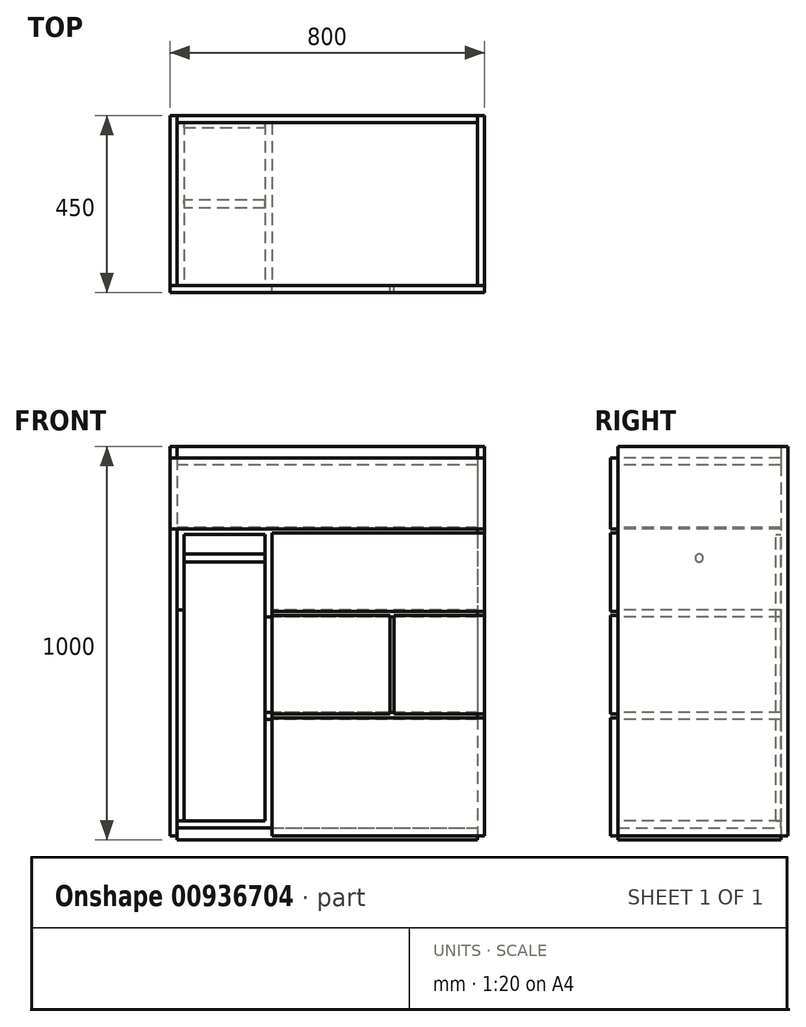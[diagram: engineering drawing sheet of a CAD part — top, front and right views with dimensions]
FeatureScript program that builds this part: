
annotation { "Feature Type Name" : "Feature", "Feature Type Description" : "" }
export const myFeature = defineFeature(function(context is Context, id is Id, definition is map)
    precondition{}
    {
        {
            var Q0;
            Q0=qCreatedBy(makeId("Top.planeOp"),FACE);
            var sketch = newSketch(context, id + "F0", { "sketchPlane" : qUnion([Q0])});
            skLineSegment(sketch, "E0.bottom", {"start": v(0, 0) * mm, "end": v(800, 0) * mm});
            skLineSegment(sketch, "E0.top", {"start": v(0, 432) * mm, "end": v(800, 432) * mm});
            skLineSegment(sketch, "E0.left", {"start": v(0, 0) * mm, "end": v(0, 432) * mm});
            skLineSegment(sketch, "E0.right", {"start": v(800, 0) * mm, "end": v(800, 432) * mm});
            skLineSegment(sketch, "E1.0", {"start": v(18, 0) * mm, "end": v(18, 432) * mm});
            skLineSegment(sketch, "E2", {"start": v(400, 467.89) * mm, "end": v(400, 549.02) * mm, "construction": true});
            skPoint(sketch, "E2.startSnap0", {"position": v(400, 432) * mm});
            skLineSegment(sketch, "E3.MirrorCS", {"start": v(782, 0) * mm, "end": v(782, 432) * mm});
            skLineSegment(sketch, "E4", {"start": v(828.28, 216) * mm, "end": v(900.38, 216) * mm, "construction": true});
            skPoint(sketch, "E4.startSnap0", {"position": v(800, 216) * mm});
            skLineSegment(sketch, "E5.0", {"start": v(0, 414) * mm, "end": v(800, 414) * mm});
            skSolve(sketch);
        }
        {
            var Q0;
            {var subQ0=sQuery(id+"F0.wireOp",EDGE,"E0.left");var subQ1=sQuery(id+"F0.wireOp",EDGE,"E0.bottom");var subQ2=makeQuery(id+"F0.imprint","INTERSECT",VERTEX,{"derivedFrom":[subQ1,subQ0]});Q0=makeQuery(id+"F0.imprint","IMPRINT",FACE,{"disambiguationData":[TD([[makeQuery(id+"F0.imprint","IMPRINT",EDGE,{"disambiguationData":[TD([[subQ2,-1.0]])],"derivedFrom":subQ1}),1.0]])]});}
            var Q1;
            {var subQ0=sQuery(id+"F0.wireOp",EDGE,"E0.left");var subQ1=sQuery(id+"F0.wireOp",EDGE,"E0.top");var subQ2=makeQuery(id+"F0.imprint","INTERSECT",VERTEX,{"derivedFrom":[subQ1,subQ0]});Q1=makeQuery(id+"F0.imprint","IMPRINT",FACE,{"disambiguationData":[TD([[makeQuery(id+"F0.imprint","IMPRINT",EDGE,{"disambiguationData":[TD([[subQ2,-1.0]])],"derivedFrom":subQ1}),-1.0]])]});}
            var Q2;
            {var subQ0=sQuery(id+"F0.wireOp",EDGE,"E0.right");var subQ1=sQuery(id+"F0.wireOp",EDGE,"E0.top");var subQ2=makeQuery(id+"F0.imprint","INTERSECT",VERTEX,{"derivedFrom":[subQ1,subQ0]});Q2=makeQuery(id+"F0.imprint","IMPRINT",FACE,{"disambiguationData":[TD([[makeQuery(id+"F0.imprint","IMPRINT",EDGE,{"disambiguationData":[TD([[subQ2,1.0]])],"derivedFrom":subQ1}),-1.0]])]});}
            var Q3;
            {var subQ0=sQuery(id+"F0.wireOp",EDGE,"E0.right");var subQ1=sQuery(id+"F0.wireOp",EDGE,"E0.bottom");var subQ2=makeQuery(id+"F0.imprint","INTERSECT",VERTEX,{"derivedFrom":[subQ1,subQ0]});Q3=makeQuery(id+"F0.imprint","IMPRINT",FACE,{"disambiguationData":[TD([[makeQuery(id+"F0.imprint","IMPRINT",EDGE,{"disambiguationData":[TD([[subQ2,1.0]])],"derivedFrom":subQ1}),1.0]])]});}
            extrude(context, id + "F1", {"entities" : qUnion([Q0, Q1, Q2, Q3]), "depth" : 990 * mm, "offsetDistance" : 25 * mm});
        }
        {
            var Q0;
            {var subQ0=sQuery(id+"F0.wireOp",EDGE,"E1.0");var subQ1=sQuery(id+"F0.wireOp",EDGE,"E0.top");var subQ2=makeQuery(id+"F0.imprint","INTERSECT",VERTEX,{"derivedFrom":[subQ1,subQ0]});Q0=makeQuery(id+"F0.imprint","IMPRINT",FACE,{"disambiguationData":[TD([[makeQuery(id+"F0.imprint","IMPRINT",EDGE,{"disambiguationData":[TD([[subQ2,-1.0]])],"derivedFrom":subQ1}),-1.0]])]});}
            var Q1;
            Q1=makeQuery(id+"F1.opExtrude","CAP_FACE",FACE,{"disambiguationData":[OSD([sQuery(id+"F0.wireOp",EDGE,"E0.bottom"),sQuery(id+"F0.wireOp",EDGE,"E0.top"),sQuery(id+"F0.wireOp",EDGE,"E0.left"),sQuery(id+"F0.wireOp",EDGE,"E1.0")])],"isStart":false});
            extrude(context, id + "F2", {"entities" : qUnion([Q0]), "endBound" : BoundingType.UP_TO_SURFACE, "depth" : 25 * mm, "endBoundEntityFace" : qUnion([Q1]), "offsetDistance" : 25 * mm});
        }
        {
            var Q0;
            {var subQ0=sQuery(id+"F0.wireOp",EDGE,"E1.0");var subQ1=sQuery(id+"F0.wireOp",EDGE,"E0.bottom");var subQ2=makeQuery(id+"F0.imprint","INTERSECT",VERTEX,{"derivedFrom":[subQ1,subQ0]});Q0=makeQuery(id+"F0.imprint","IMPRINT",FACE,{"disambiguationData":[TD([[makeQuery(id+"F0.imprint","IMPRINT",EDGE,{"disambiguationData":[TD([[subQ2,-1.0]])],"derivedFrom":subQ1}),1.0]])]});}
            extrude(context, id + "F3", {"entities" : qUnion([Q0]), "depth" : 20 * mm, "offsetDistance" : 25 * mm, "hasSecondDirection" : true, "secondDirectionOppositeDirection" : true, "secondDirectionDepth" : 10 * mm});
        }
        {
            var Q0;
            {var subQ0=sQuery(id+"F0.wireOp",EDGE,"E0.bottom");Q0=makeQuery(id+"F1.opExtrude","SWEPT_FACE",FACE,{"disambiguationData":[OSD([subQ0]),TDD([makeQuery(id+"F0.imprint","IMPRINT",EDGE,{"disambiguationData":[TD([[makeQuery(id+"F0.imprint","INTERSECT",VERTEX,{"derivedFrom":[subQ0,sQuery(id+"F0.wireOp",EDGE,"E0.left")]}),-1.0]])],"derivedFrom":subQ0})])]});}
            var sketch = newSketch(context, id + "F4", { "sketchPlane" : qUnion([Q0])});
            skLineSegment(sketch, "E6.bottom", {"start": v(800, 560) * mm, "end": v(570, 560) * mm});
            skLineSegment(sketch, "E6.top", {"start": v(800, 310) * mm, "end": v(570, 310) * mm});
            skLineSegment(sketch, "E6.left", {"start": v(800, 560) * mm, "end": v(800, 310) * mm});
            skLineSegment(sketch, "E6.right", {"start": v(570, 560) * mm, "end": v(570, 310) * mm});
            skLineSegment(sketch, "E7.bottom", {"start": v(560, 560) * mm, "end": v(0, 560) * mm});
            skLineSegment(sketch, "E7.top", {"start": v(560, 310) * mm, "end": v(0, 310) * mm});
            skLineSegment(sketch, "E7.left", {"start": v(560, 560) * mm, "end": v(560, 310) * mm});
            skLineSegment(sketch, "E7.right", {"start": v(0, 560) * mm, "end": v(0, 310) * mm});
            skLineSegment(sketch, "E8", {"start": v(570, 435) * mm, "end": v(560, 435) * mm, "construction": true});
            skLineSegment(sketch, "E9.bottom", {"start": v(0, 300) * mm, "end": v(250, 300) * mm});
            skLineSegment(sketch, "E9.top", {"start": v(0, 0) * mm, "end": v(250, 0) * mm});
            skLineSegment(sketch, "E9.right", {"start": v(250, 300) * mm, "end": v(250, 0) * mm});
            skLineSegment(sketch, "E10.bottom", {"start": v(260, 300) * mm, "end": v(800, 300) * mm});
            skLineSegment(sketch, "E10.top", {"start": v(260, 0) * mm, "end": v(800, 0) * mm});
            skLineSegment(sketch, "E10.left", {"start": v(260, 300) * mm, "end": v(260, 0) * mm});
            skLineSegment(sketch, "E10.right", {"start": v(800, 300) * mm, "end": v(800, 0) * mm});
            skLineSegment(sketch, "E11", {"start": v(10.26, 310) * mm, "end": v(10.26, 300) * mm, "construction": true});
            skLineSegment(sketch, "E12", {"start": v(260, 150) * mm, "end": v(250, 150) * mm, "construction": true});
            skLineSegment(sketch, "E13.bottom", {"start": v(800, 770) * mm, "end": v(260, 770) * mm});
            skLineSegment(sketch, "E13.top", {"start": v(800, 570) * mm, "end": v(260, 570) * mm});
            skLineSegment(sketch, "E13.left", {"start": v(800, 770) * mm, "end": v(800, 570) * mm});
            skLineSegment(sketch, "E13.right", {"start": v(260, 770) * mm, "end": v(260, 570) * mm});
            skLineSegment(sketch, "E14.bottom", {"start": v(250, 770) * mm, "end": v(0, 770) * mm});
            skLineSegment(sketch, "E14.top", {"start": v(250, 570) * mm, "end": v(0, 570) * mm});
            skLineSegment(sketch, "E14.left", {"start": v(250, 770) * mm, "end": v(250, 570) * mm});
            skLineSegment(sketch, "E14.right", {"start": v(0, 770) * mm, "end": v(0, 570) * mm});
            skLineSegment(sketch, "E15", {"start": v(277.64, 570) * mm, "end": v(277.64, 560) * mm, "construction": true});
            skLineSegment(sketch, "E16", {"start": v(260, 629.54) * mm, "end": v(250, 629.54) * mm, "construction": true});
            skLineSegment(sketch, "E17.bottom", {"start": v(0, 990) * mm, "end": v(800, 990) * mm});
            skLineSegment(sketch, "E17.top", {"start": v(0, 780) * mm, "end": v(800, 780) * mm});
            skLineSegment(sketch, "E17.left", {"start": v(0, 990) * mm, "end": v(0, 780) * mm});
            skLineSegment(sketch, "E17.right", {"start": v(800, 990) * mm, "end": v(800, 780) * mm});
            skLineSegment(sketch, "E18", {"start": v(-67.03, 780) * mm, "end": v(-67.03, 770) * mm, "construction": true});
            skLineSegment(sketch, "E19", {"start": v(0, 300) * mm, "end": v(0, 0) * mm});
            skLineSegment(sketch, "E20", {"start": v(0, 960) * mm, "end": v(800, 960) * mm});
            skLineSegment(sketch, "E21", {"start": v(260, 560) * mm, "end": v(260, 310) * mm});
            skSolve(sketch);
        }
        {
            var Q0;
            {var subQ0=sQuery(id+"F4.wireOp",EDGE,"E17.right");var subQ1=sQuery(id+"F4.wireOp",EDGE,"E17.top");var subQ2=makeQuery(id+"F4.imprint","INTERSECT",VERTEX,{"derivedFrom":[subQ1,subQ0]});Q0=makeQuery(id+"F4.imprint","IMPRINT",FACE,{"disambiguationData":[TD([[makeQuery(id+"F4.imprint","IMPRINT",EDGE,{"disambiguationData":[TD([[subQ2,1.0]])],"derivedFrom":subQ0}),-1.0]])]});}
            var Q1;
            {var subQ0=sQuery(id+"F4.wireOp",EDGE,"E17.left");var subQ6=sQuery(id+"F4.wireOp",EDGE,"E20");var subQ7=makeQuery(id+"F4.imprint","INTERSECT",VERTEX,{"derivedFrom":[subQ0,subQ6]});Q1=makeQuery(id+"F4.imprint","IMPRINT",FACE,{"disambiguationData":[TD([[makeQuery(id+"F4.imprint","IMPRINT",EDGE,{"disambiguationData":[TD([[subQ7,-1.0]])],"derivedFrom":subQ6}),-1.0]])]});}
            var Q2;
            Q2=makeQuery(id+"F4.imprint","IMPRINT",FACE,{"disambiguationData":[TD([[makeQuery(id+"F4.imprint","IMPRINT",EDGE,{"derivedFrom":sQuery(id+"F4.wireOp",EDGE,"E13.bottom")}),1.0]])]});
            var Q3;
            Q3=makeQuery(id+"F4.imprint","IMPRINT",FACE,{"disambiguationData":[TD([[makeQuery(id+"F4.imprint","IMPRINT",EDGE,{"derivedFrom":sQuery(id+"F4.wireOp",EDGE,"E6.bottom")}),1.0]])]});
            var Q4;
            Q4=makeQuery(id+"F4.imprint","IMPRINT",FACE,{"disambiguationData":[TD([[makeQuery(id+"F4.imprint","IMPRINT",EDGE,{"derivedFrom":sQuery(id+"F4.wireOp",EDGE,"E10.bottom")}),-1.0]])]});
            var Q5;
            {var subQ0=sQuery(id+"F4.wireOp",EDGE,"E7.left");Q5=makeQuery(id+"F4.imprint","IMPRINT",FACE,{"disambiguationData":[TD([[makeQuery(id+"F4.imprint","IMPRINT",EDGE,{"derivedFrom":subQ0}),-1.0]])]});}
            extrude(context, id + "F5", {"entities" : qUnion([Q0, Q1, Q2, Q3, Q4, Q5]), "depth" : 18 * mm, "offsetDistance" : 25 * mm});
        }
        {
            var Q0;
            Q0=makeQuery(id+"F5.opExtrude","CAP_FACE",FACE,{"disambiguationData":[OSD([sQuery(id+"F4.wireOp",EDGE,"E17.top"),sQuery(id+"F4.wireOp",EDGE,"E17.left"),sQuery(id+"F4.wireOp",EDGE,"E17.right"),sQuery(id+"F4.wireOp",EDGE,"E20")])],"isStart":true});
            var sketch = newSketch(context, id + "F6", { "sketchPlane" : qUnion([Q0])});
            skLineSegment(sketch, "E22.bottom", {"start": v(-782, 784) * mm, "end": v(-18, 784) * mm});
            skLineSegment(sketch, "E22.top", {"start": v(-782, 766) * mm, "end": v(-18, 766) * mm});
            skLineSegment(sketch, "E22.left", {"start": v(-782, 784) * mm, "end": v(-782, 766) * mm});
            skLineSegment(sketch, "E22.right", {"start": v(-18, 784) * mm, "end": v(-18, 766) * mm});
            skLineSegment(sketch, "E23", {"start": v(-903.66, 780) * mm, "end": v(-903.66, 770) * mm, "construction": true});
            skLineSegment(sketch, "E24", {"start": v(-878.2, 570) * mm, "end": v(-878.2, 560) * mm, "construction": true});
            skLineSegment(sketch, "E25", {"start": v(-871.46, 310) * mm, "end": v(-871.46, 300) * mm, "construction": true});
            skLineSegment(sketch, "E26", {"start": v(-570, 442.76) * mm, "end": v(-560, 442.76) * mm, "construction": true});
            skLineSegment(sketch, "E27", {"start": v(-260, 157.99) * mm, "end": v(-242, 157.99) * mm, "construction": true});
            skPoint(sketch, "E28", {"position": v(-903.66, 775) * mm});
            skPoint(sketch, "E29", {"position": v(-878.2, 565) * mm});
            skPoint(sketch, "E30", {"position": v(-565, 442.76) * mm});
            skPoint(sketch, "E31", {"position": v(-871.46, 305) * mm});
            skPoint(sketch, "E32", {"position": v(-251, 157.99) * mm});
            skPoint(sketch, "E33", {"position": v(-782, 775) * mm});
            skLineSegment(sketch, "E34.bottom", {"start": v(-782, 574) * mm, "end": v(-18, 574) * mm});
            skLineSegment(sketch, "E34.top", {"start": v(-782, 556) * mm, "end": v(-18, 556) * mm});
            skLineSegment(sketch, "E34.left", {"start": v(-782, 574) * mm, "end": v(-782, 556) * mm});
            skLineSegment(sketch, "E34.right", {"start": v(-18, 574) * mm, "end": v(-18, 556) * mm});
            skLineSegment(sketch, "E35.bottom", {"start": v(-782, 314) * mm, "end": v(-18, 314) * mm});
            skLineSegment(sketch, "E35.top", {"start": v(-782, 296) * mm, "end": v(-18, 296) * mm});
            skLineSegment(sketch, "E35.left", {"start": v(-782, 314) * mm, "end": v(-782, 296) * mm});
            skLineSegment(sketch, "E35.right", {"start": v(-18, 314) * mm, "end": v(-18, 296) * mm});
            skLineSegment(sketch, "E36.bottom", {"start": v(-260, 296) * mm, "end": v(-242, 296) * mm});
            skLineSegment(sketch, "E36.top", {"start": v(-260, 20) * mm, "end": v(-242, 20) * mm});
            skLineSegment(sketch, "E36.left", {"start": v(-260, 296) * mm, "end": v(-260, 20) * mm});
            skLineSegment(sketch, "E36.right", {"start": v(-242, 296) * mm, "end": v(-242, 20) * mm});
            skLineSegment(sketch, "E37.bottom", {"start": v(-574, 556) * mm, "end": v(-556, 556) * mm});
            skLineSegment(sketch, "E37.top", {"start": v(-574, 314) * mm, "end": v(-556, 314) * mm});
            skLineSegment(sketch, "E37.left", {"start": v(-574, 556) * mm, "end": v(-574, 314) * mm});
            skLineSegment(sketch, "E37.right", {"start": v(-556, 556) * mm, "end": v(-556, 314) * mm});
            skLineSegment(sketch, "E38.bottom", {"start": v(-260, 766) * mm, "end": v(-242, 766) * mm});
            skLineSegment(sketch, "E38.top", {"start": v(-260, 574) * mm, "end": v(-242, 574) * mm});
            skLineSegment(sketch, "E38.left", {"start": v(-260, 766) * mm, "end": v(-260, 574) * mm});
            skLineSegment(sketch, "E38.right", {"start": v(-242, 766) * mm, "end": v(-242, 574) * mm});
            skLineSegment(sketch, "E39.bottom", {"start": v(-36, 766) * mm, "end": v(-18, 766) * mm});
            skLineSegment(sketch, "E39.top", {"start": v(-36, 574) * mm, "end": v(-18, 574) * mm});
            skLineSegment(sketch, "E39.left", {"start": v(-36, 766) * mm, "end": v(-36, 574) * mm});
            skLineSegment(sketch, "E39.right", {"start": v(-18, 766) * mm, "end": v(-18, 574) * mm});
            skPoint(sketch, "E40", {"position": v(-782, 565) * mm});
            skPoint(sketch, "E41", {"position": v(-565, 556) * mm});
            skPoint(sketch, "E42", {"position": v(-782, 305) * mm});
            skPoint(sketch, "E43", {"position": v(-251, 296) * mm});
            skLineSegment(sketch, "E44.bottom", {"start": v(-782, 960) * mm, "end": v(-18, 960) * mm});
            skLineSegment(sketch, "E44.top", {"start": v(-782, 942) * mm, "end": v(-18, 942) * mm});
            skLineSegment(sketch, "E44.left", {"start": v(-782, 960) * mm, "end": v(-782, 942) * mm});
            skLineSegment(sketch, "E44.right", {"start": v(-18, 960) * mm, "end": v(-18, 942) * mm});
            skLineSegment(sketch, "E45", {"start": v(-260, 574) * mm, "end": v(-260, 296) * mm});
            skLineSegment(sketch, "E46", {"start": v(-242, 574) * mm, "end": v(-242, 296) * mm});
            skLineSegment(sketch, "E47", {"start": v(-36, 574) * mm, "end": v(-36, 20) * mm});
            skLineSegment(sketch, "E48", {"start": v(-36, 20) * mm, "end": v(-18, 20) * mm});
            skLineSegment(sketch, "E49", {"start": v(-18, 20) * mm, "end": v(-18, 556) * mm});
            skLineSegment(sketch, "E50", {"start": v(-260, 38) * mm, "end": v(-18, 38) * mm});
            skLineSegment(sketch, "E51", {"start": v(-260, 20) * mm, "end": v(-18, 20) * mm});
            skSolve(sketch);
        }
        {
            var Q0;
            Q0=makeQuery(id+"F6.imprint","IMPRINT",FACE,{"disambiguationData":[TD([[makeQuery(id+"F6.imprint","IMPRINT",EDGE,{"derivedFrom":sQuery(id+"F6.wireOp",EDGE,"E44.bottom")}),1.0]])]});
            var Q1;
            {var subQ6=sQuery(id+"F6.wireOp",EDGE,"E38.bottom");Q1=makeQuery(id+"F6.imprint","IMPRINT",FACE,{"disambiguationData":[TD([[makeQuery(id+"F6.imprint","IMPRINT",EDGE,{"derivedFrom":subQ6}),1.0]])]});}
            var Q2;
            {var subQ0=sQuery(id+"F6.wireOp",EDGE,"E22.bottom");Q2=makeQuery(id+"F6.imprint","IMPRINT",FACE,{"disambiguationData":[TD([[makeQuery(id+"F6.imprint","IMPRINT",EDGE,{"derivedFrom":subQ0}),-1.0]])]});}
            var Q3;
            {var subQ4=sQuery(id+"F6.wireOp",EDGE,"E34.left");Q3=makeQuery(id+"F6.imprint","IMPRINT",FACE,{"disambiguationData":[TD([[makeQuery(id+"F6.imprint","IMPRINT",EDGE,{"derivedFrom":subQ4}),1.0]])]});}
            var Q4;
            {var subQ3=sQuery(id+"F6.wireOp",EDGE,"E35.left");Q4=makeQuery(id+"F6.imprint","IMPRINT",FACE,{"disambiguationData":[TD([[makeQuery(id+"F6.imprint","IMPRINT",EDGE,{"derivedFrom":subQ3}),1.0]])]});}
            var Q5;
            Q5=makeQuery(id+"F6.imprint","IMPRINT",FACE,{"disambiguationData":[TD([[makeQuery(id+"F6.imprint","IMPRINT",EDGE,{"derivedFrom":sQuery(id+"F6.wireOp",EDGE,"QM6Bufxx-I5ZU-JCkN-k9jX-k9IJHGgFzfra.bottom")}),1.0]])]});
            var Q6;
            {var subQ0=sQuery(id+"F6.wireOp",EDGE,"E51");var subQ1=sQuery(id+"F6.wireOp",EDGE,"E36.left");var subQ2=makeQuery(id+"F6.imprint","INTERSECT",VERTEX,{"derivedFrom":[subQ1,subQ0]});Q6=makeQuery(id+"F6.imprint","IMPRINT",FACE,{"disambiguationData":[TD([[makeQuery(id+"F6.imprint","IMPRINT",EDGE,{"disambiguationData":[TD([[subQ2,1.0]])],"derivedFrom":subQ1}),1.0]])]});}
            var Q7;
            {var subQ0=sQuery(id+"F6.wireOp",EDGE,"E51");var subQ1=sQuery(id+"F6.wireOp",EDGE,"E36.right");var subQ2=makeQuery(id+"F6.imprint","INTERSECT",VERTEX,{"derivedFrom":[subQ1,subQ0]});Q7=makeQuery(id+"F6.imprint","IMPRINT",FACE,{"disambiguationData":[TD([[makeQuery(id+"F6.imprint","IMPRINT",EDGE,{"disambiguationData":[TD([[subQ2,1.0]])],"derivedFrom":subQ1}),1.0]])]});}
            var Q8;
            {var subQ0=sQuery(id+"F6.wireOp",EDGE,"E51");var subQ1=sQuery(id+"F6.wireOp",EDGE,"E47");var subQ2=makeQuery(id+"F6.imprint","INTERSECT",VERTEX,{"derivedFrom":[subQ1,subQ0]});Q8=makeQuery(id+"F6.imprint","IMPRINT",FACE,{"disambiguationData":[TD([[makeQuery(id+"F6.imprint","IMPRINT",EDGE,{"disambiguationData":[TD([[subQ2,1.0]])],"derivedFrom":subQ1}),1.0]])]});}
            var Q9;
            Q9=makeQuery(id+"F2.opExtrude","SWEPT_FACE",FACE,{"disambiguationData":[OSD([sQuery(id+"F0.wireOp",EDGE,"E5.0")])]});
            extrude(context, id + "F7", {"entities" : qUnion([Q0, Q1, Q2, Q3, Q4, Q5, Q6, Q7, Q8]), "endBound" : BoundingType.UP_TO_SURFACE, "depth" : 25 * mm, "endBoundEntityFace" : qUnion([Q9]), "offsetDistance" : 25 * mm});
        }
        {
            var Q0;
            Q0=makeQuery(id+"F6.imprint","IMPRINT",FACE,{"disambiguationData":[TD([[makeQuery(id+"F6.imprint","IMPRINT",EDGE,{"derivedFrom":sQuery(id+"F6.wireOp",EDGE,"E38.bottom")}),-1.0]])]});
            var Q1;
            Q1=makeQuery(id+"F6.imprint","IMPRINT",FACE,{"disambiguationData":[TD([[makeQuery(id+"F6.imprint","IMPRINT",EDGE,{"derivedFrom":sQuery(id+"F6.wireOp",EDGE,"E37.bottom")}),-1.0]])]});
            var Q2;
            Q2=makeQuery(id+"F6.imprint","IMPRINT",FACE,{"disambiguationData":[TD([[makeQuery(id+"F6.imprint","IMPRINT",EDGE,{"derivedFrom":sQuery(id+"F6.wireOp",EDGE,"E36.bottom")}),-1.0]])]});
            var Q3;
            Q3=makeQuery(id+"F6.imprint","IMPRINT",FACE,{"disambiguationData":[TD([[makeQuery(id+"F6.imprint","IMPRINT",EDGE,{"derivedFrom":sQuery(id+"F6.wireOp",EDGE,"E39.bottom")}),-1.0]])]});
            var Q4;
            {var subQ5=sQuery(id+"F6.wireOp",EDGE,"E36.bottom");Q4=makeQuery(id+"F6.imprint","IMPRINT",FACE,{"disambiguationData":[TD([[makeQuery(id+"F6.imprint","IMPRINT",EDGE,{"derivedFrom":subQ5}),1.0]])]});}
            var Q5;
            {var subQ0=sQuery(id+"F6.wireOp",EDGE,"E45");var subQ1=sQuery(id+"F6.wireOp",EDGE,"E34.top");var subQ2=makeQuery(id+"F6.imprint","INTERSECT",VERTEX,{"derivedFrom":[subQ1,subQ0]});Q5=makeQuery(id+"F6.imprint","IMPRINT",FACE,{"disambiguationData":[TD([[makeQuery(id+"F6.imprint","IMPRINT",EDGE,{"disambiguationData":[TD([[subQ2,-1.0]])],"derivedFrom":subQ1}),-1.0]])]});}
            var Q6;
            {var subQ5=sQuery(id+"F6.wireOp",EDGE,"E38.top");Q6=makeQuery(id+"F6.imprint","IMPRINT",FACE,{"disambiguationData":[TD([[makeQuery(id+"F6.imprint","IMPRINT",EDGE,{"derivedFrom":subQ5}),-1.0]])]});}
            var Q7;
            {var subQ0=sQuery(id+"F6.wireOp",EDGE,"E34.right");Q7=makeQuery(id+"F6.imprint","IMPRINT",FACE,{"disambiguationData":[TD([[makeQuery(id+"F6.imprint","IMPRINT",EDGE,{"derivedFrom":subQ0}),-1.0]])]});}
            var Q8;
            {var subQ0=sQuery(id+"F6.wireOp",EDGE,"E49");var subQ5=sQuery(id+"F6.wireOp",EDGE,"E35.bottom");var subQ7=makeQuery(id+"F6.imprint","INTERSECT",VERTEX,{"derivedFrom":[subQ5,subQ0]});Q8=makeQuery(id+"F6.imprint","IMPRINT",FACE,{"disambiguationData":[TD([[makeQuery(id+"F6.imprint","IMPRINT",EDGE,{"disambiguationData":[TD([[subQ7,1.0]])],"derivedFrom":subQ5}),1.0]])]});}
            var Q9;
            {var subQ0=sQuery(id+"F6.wireOp",EDGE,"E49");var subQ1=sQuery(id+"F6.wireOp",EDGE,"E35.bottom");var subQ2=makeQuery(id+"F6.imprint","INTERSECT",VERTEX,{"derivedFrom":[subQ1,subQ0]});Q9=makeQuery(id+"F6.imprint","IMPRINT",FACE,{"disambiguationData":[TD([[makeQuery(id+"F6.imprint","IMPRINT",EDGE,{"disambiguationData":[TD([[subQ2,1.0]])],"derivedFrom":subQ1}),-1.0]])]});}
            var Q10;
            {var subQ0=sQuery(id+"F6.wireOp",EDGE,"E49");var subQ1=sQuery(id+"F6.wireOp",EDGE,"E35.top");var subQ2=makeQuery(id+"F6.imprint","INTERSECT",VERTEX,{"derivedFrom":[subQ1,subQ0]});Q10=makeQuery(id+"F6.imprint","IMPRINT",FACE,{"disambiguationData":[TD([[makeQuery(id+"F6.imprint","IMPRINT",EDGE,{"disambiguationData":[TD([[subQ2,1.0]])],"derivedFrom":subQ1}),-1.0]])]});}
            var Q11;
            Q11=makeQuery(id+"F7.opExtrude","CAP_FACE",FACE,{"disambiguationData":[OSD([sQuery(id+"F6.wireOp",EDGE,"E34.bottom"),sQuery(id+"F6.wireOp",EDGE,"E34.top"),sQuery(id+"F6.wireOp",EDGE,"E34.left"),sQuery(id+"F6.wireOp",EDGE,"E34.right"),sQuery(id+"F6.wireOp",EDGE,"E37.bottom"),sQuery(id+"F6.wireOp",EDGE,"E38.top"),sQuery(id+"F6.wireOp",EDGE,"E39.top")])],"isStart":false});
            extrude(context, id + "F8", {"entities" : qUnion([Q0, Q1, Q2, Q3, Q4, Q5, Q6, Q7, Q8, Q9, Q10]), "endBound" : BoundingType.UP_TO_SURFACE, "depth" : 25 * mm, "endBoundEntityFace" : qUnion([Q11]), "offsetDistance" : 25 * mm});
        }
        {
            var Q0;
            Q0=makeQuery(id+"F8.opExtrude","SWEPT_FACE",FACE,{"disambiguationData":[OSD([sQuery(id+"F6.wireOp",EDGE,"E39.left"),sQuery(id+"F6.wireOp",EDGE,"E47")])]});
            var sketch = newSketch(context, id + "F9", { "sketchPlane" : qUnion([Q0])});
            skLineSegment(sketch, "E52", {"start": v(207, 766) * mm, "end": v(207, 706) * mm, "construction": true});
            skCircle(sketch, "E53", {"center": v(207, 706) * mm, "radius": 10 * mm});
            skPoint(sketch, "E54", {"position": v(207, 766) * mm});
            skSolve(sketch);
        }
        {
            var Q0;
            Q0=makeQuery(id+"F9.imprint","IMPRINT",FACE,{"disambiguationData":[TD([[makeQuery(id+"F9.imprint","IMPRINT",EDGE,{"derivedFrom":sQuery(id+"F9.wireOp",EDGE,"E53")}),1.0]])]});
            var Q1;
            Q1=sQuery(id+"F9.wireOp",EDGE,"E53");
            var Q2;
            Q2=makeQuery(id+"F8.opExtrude","SWEPT_FACE",FACE,{"disambiguationData":[OSD([sQuery(id+"F6.wireOp",EDGE,"E36.right"),sQuery(id+"F6.wireOp",EDGE,"E38.right"),sQuery(id+"F6.wireOp",EDGE,"E46")])]});
            extrude(context, id + "F10", {"entities" : qUnion([Q0]), "surfaceEntities" : qUnion([Q1]), "endBound" : BoundingType.UP_TO_SURFACE, "depth" : 25 * mm, "endBoundEntityFace" : qUnion([Q2]), "offsetDistance" : 25 * mm});
        }
        {
            var Q0;
            Q0=makeQuery(id+"F2.opExtrude","SWEPT_FACE",FACE,{"disambiguationData":[OSD([sQuery(id+"F0.wireOp",EDGE,"E5.0")])]});
            var sketch = newSketch(context, id + "F11", { "sketchPlane" : qUnion([Q0])});
            skLineSegment(sketch, "E55.bottom", {"start": v(36, 38) * mm, "end": v(242, 38) * mm});
            skLineSegment(sketch, "E55.top", {"start": v(36, 766) * mm, "end": v(242, 766) * mm});
            skLineSegment(sketch, "E55.left", {"start": v(36, 38) * mm, "end": v(36, 766) * mm});
            skLineSegment(sketch, "E55.right", {"start": v(242, 38) * mm, "end": v(242, 766) * mm});
            skSolve(sketch);
        }
        {
            var Q0;
            Q0=makeQuery(id+"F11.imprint","IMPRINT",FACE,{"disambiguationData":[TD([[makeQuery(id+"F11.imprint","IMPRINT",EDGE,{"derivedFrom":sQuery(id+"F11.wireOp",EDGE,"E55.bottom")}),1.0]])]});
            extrude(context, id + "F12", {"entities" : qUnion([Q0]), "depth" : 12 * mm, "offsetDistance" : 25 * mm});
        }
    });
